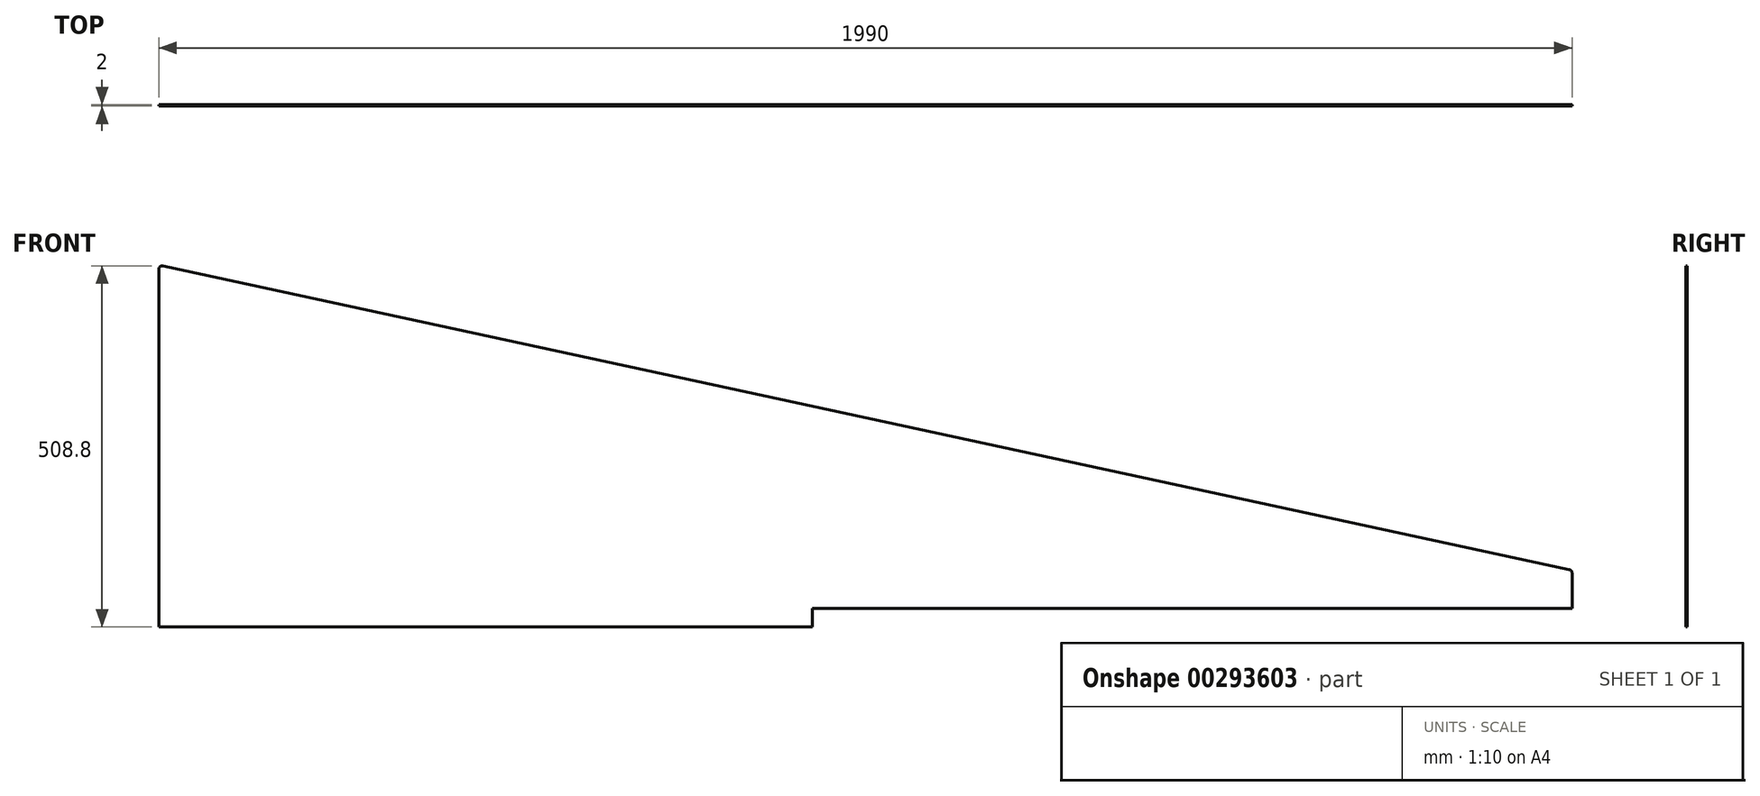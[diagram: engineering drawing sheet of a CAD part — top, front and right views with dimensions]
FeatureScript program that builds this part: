
annotation { "Feature Type Name" : "Feature", "Feature Type Description" : "" }
export const myFeature = defineFeature(function(context is Context, id is Id, definition is map)
    precondition{}
    {
        {
            var Q0;
            Q0=qCreatedBy(makeId("Front.planeOp"),FACE);
            var sketch = newSketch(context, id + "F0", { "sketchPlane" : qUnion([Q0])});
            skLineSegment(sketch, "E0.bottom", {"start": v(0, 0) * mm, "end": v(-1990, 0) * mm, "construction": true});
            skLineSegment(sketch, "E0.left", {"start": v(0, 0) * mm, "end": v(0, 20) * mm});
            skLineSegment(sketch, "E0.right", {"start": v(-1990, 0) * mm, "end": v(-1990, 443.8) * mm});
            skLineSegment(sketch, "E1", {"start": v(-1983.94, 448.7) * mm, "end": v(-3.94, 20.85) * mm});
            skLineSegment(sketch, "E2", {"start": v(-1990, 0) * mm, "end": v(-1990, -60) * mm});
            skLineSegment(sketch, "E3", {"start": v(-1990, -60) * mm, "end": v(-1070, -60) * mm});
            skLineSegment(sketch, "E4", {"start": v(-1070, -60) * mm, "end": v(-1070, -34) * mm});
            skLineSegment(sketch, "E5", {"start": v(-1070, -34) * mm, "end": v(0, -34) * mm});
            skLineSegment(sketch, "E6", {"start": v(0, -34) * mm, "end": v(0, 15.97) * mm});
            skPoint(sketch, "E7.visualSharp", {"position": v(-1990, 450) * mm});
            skArc(sketch, "E7.filletArc", {"start": v(-1983.94, 448.7) * mm, "mid": v(-1988.14, 447.7) * mm, "end": v(-1990, 443.8) * mm});
            skPoint(sketch, "E8.visualSharp", {"position": v(0, 20) * mm});
            skArc(sketch, "E8.filletArc", {"start": v(0, 15.97) * mm, "mid": v(-1.1, 19.1) * mm, "end": v(-3.94, 20.85) * mm});
            skSolve(sketch);
        }
        {
            var Q0;
            Q0=makeQuery(id+"F0.imprint","IMPRINT",FACE,{"disambiguationData":[TD([[makeQuery(id+"F0.imprint","IMPRINT",EDGE,{"derivedFrom":sQuery(id+"F0.wireOp",EDGE,"E0.right")}),-1.0]])]});
            extrude(context, id + "F1", {"entities" : qUnion([Q0]), "depth" : 2 * mm});
        }
    });
